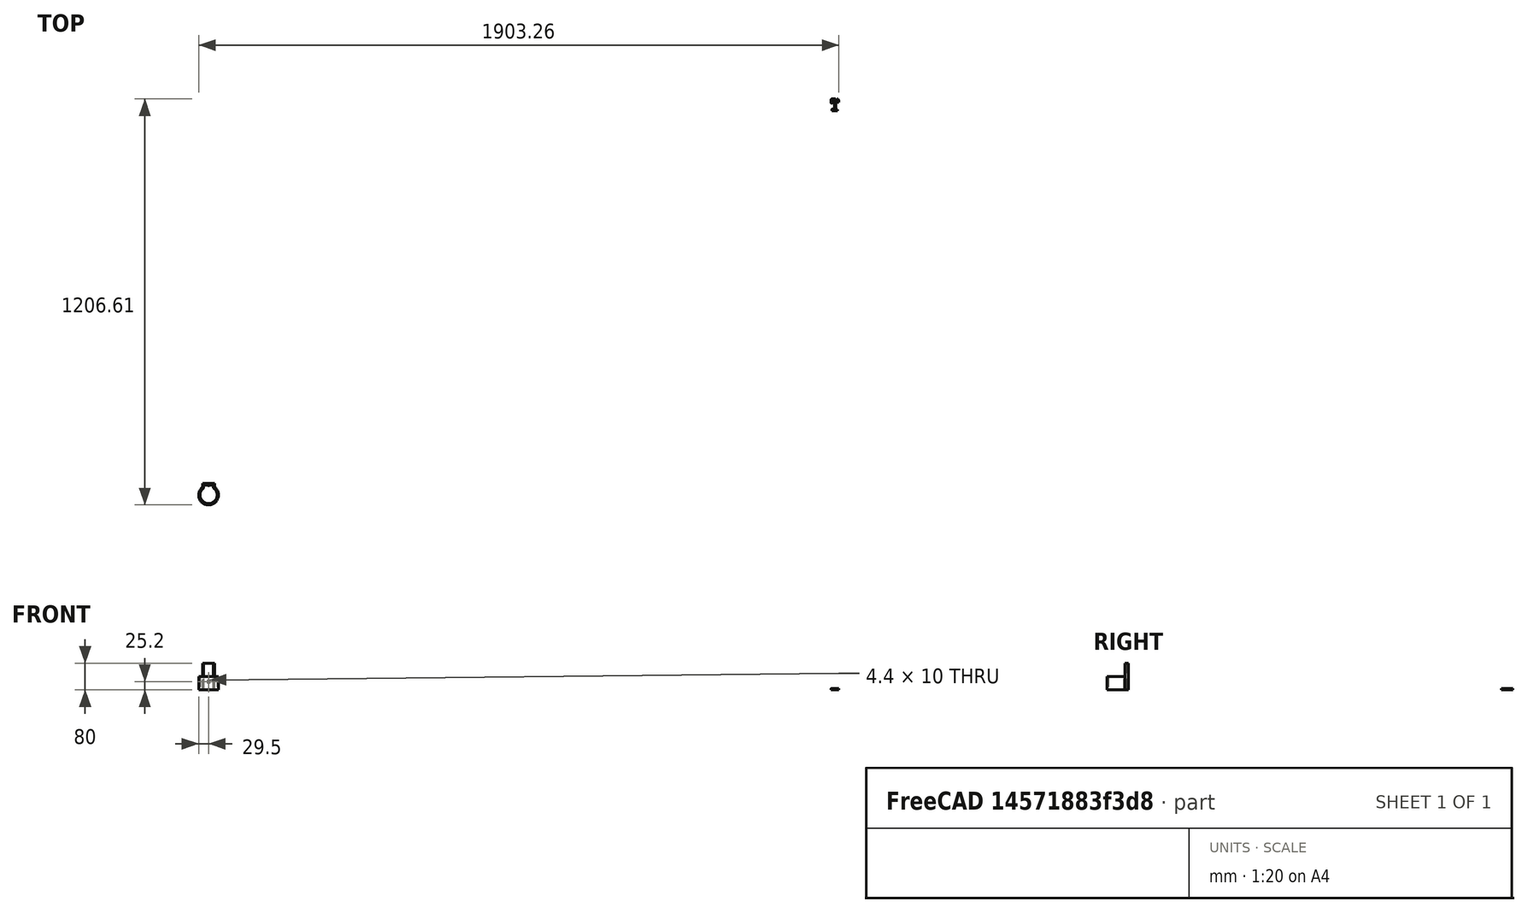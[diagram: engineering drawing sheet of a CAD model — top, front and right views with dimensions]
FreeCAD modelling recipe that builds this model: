
FCSTD DOCUMENT  (FreeCAD 1.2R44861 (Git))
Label: SkadisCylinderHolder
License: All rights reserved
LicenseURL: https://en.wikipedia.org/wiki/All_rights_reserved
objects: PartDesign::Pad×6, Sketcher::SketchObject×5, PartDesign::Pocket×3, Part::Feature×2, PartDesign::Chamfer×2, App::Point×1, Mesh::Feature×1, Part::Refine×1, PartDesign::Body×1
note: 47 computed .brp shape members not serialized (recipe doc carries the construction recipe); baked Part::Feature solids carry a one-line shape summary decoded from their .brp

FEATURE [App::Point] Origin001
  Role = Origin
FEATURE [Mesh::Feature] Skadis_Universal_Hook_1
FEATURE [Part::Feature] Skadis_Universal_Hook_001
  shape: bbox 23.2 x 35 x 4.5 mm, 9836 faces, 0 solids (baked)
FEATURE [Part::Feature] Skadis_Universal_Hook_001_solid  label="Skadis_Universal_Hook_001 (Solid)"
  shape: bbox 23.2 x 35 x 4.5 mm, 9836 faces (baked)
FEATURE [Part::Refine] Skadis_Universal_Hook_001_solid001  label="Skadis_Universal_Hook_001 (Solid)001"
  Source = -> Skadis_Universal_Hook_001_solid
FEATURE [Sketcher::SketchObject] Sketch
  ArcFitTolerance = 1e-06
  AttachmentSupport = -> [Origin]
  ExternalTypes = [0]
  FullyConstrained = true
  MakeInternals = false
  MapMode = 5
  sketch-geometry (4):
    g0: ArcOfCircle CenterX=0 CenterY=0 CenterZ=0 NormalX=0 NormalY=0 NormalZ=1 AngleXU=0 Radius=25.5 StartAngle=2.18166 EndAngle=7.24312
    g1: ArcOfCircle CenterX=0 CenterY=0 CenterZ=0 NormalX=0 NormalY=0 NormalZ=1 AngleXU=0 Radius=29.5 StartAngle=2.08956 EndAngle=7.33522
    g2: LineSegment StartX=-14.6262 StartY=20.8884 StartZ=0 EndX=-14.6262 EndY=25.6188 EndZ=0
    g3: LineSegment StartX=14.6262 StartY=20.8884 StartZ=0 EndX=14.6262 EndY=25.6188 EndZ=0
  constraints (12):
    c: Radius(g0) = 25.5
    c: Angle(g0) = 5.06145
    c: Horizontal(g0,g0)
    c: Coincident(g0,g-1)
    c: Coincident(g1,g0)
    c: Horizontal(g1,g1)
    c: Vertical(g0,g1)
    c: Distance(g1,g0) = 4
    c: Coincident(g2,g0)
    c: Coincident(g2,g1)
    c: Coincident(g3,g0)
    c: Coincident(g3,g1)
FEATURE [PartDesign::Pad] Pad
  Direction = (0,0,1)
  Length = 40
  Length2 = 10
  Profile = -> Sketch
  ReferenceAxis = -> Sketch [N_Axis]
  Refine = true
  SideType = 0
  Suppressed = false
  Type = 0
  Type2 = 0
FEATURE [Sketcher::SketchObject] Sketch001
  ArcFitTolerance = 1e-06
  AttachmentSupport = -> [Origin]
  ExternalGeometry = -> [Pad]
  ExternalTypes = [0]
  FullyConstrained = true
  MakeInternals = false
  MapMode = 5
  sketch-geometry (4):
    g0: LineSegment StartX=-18.1527 StartY=27.8536 StartZ=0 EndX=-18.1527 EndY=23.2536 EndZ=0
    g1: LineSegment StartX=-18.1527 StartY=23.2536 StartZ=0 EndX=18.1527 EndY=23.2536 EndZ=0
    g2: LineSegment StartX=18.1527 StartY=23.2536 StartZ=0 EndX=18.1527 EndY=27.8536 EndZ=0
    g3: LineSegment StartX=18.1527 StartY=27.8536 StartZ=0 EndX=-18.1527 EndY=27.8536 EndZ=0
  constraints (11):
    c: Coincident(g0,g1)
    c: Coincident(g1,g2)
    c: Coincident(g2,g3)
    c: Coincident(g3,g0)
    c: Vertical(g0)
    c: Vertical(g2)
    c: Horizontal(g3)
    c: PointOnObject(g1,g-6)
    c: Symmetric(g-6,g-5,g1)
    c: PointOnObject(g0,g-6)
    c: DistanceY(g0,g0) = 4.6
FEATURE [PartDesign::Pad] Pad001
  BaseFeature = -> Pad
  Direction = (0,0,1)
  Length = 80
  Length2 = 10
  Profile = -> Sketch001
  ReferenceAxis = -> Sketch001 [N_Axis]
  Refine = true
  SideType = 0
  Suppressed = false
  Type = 0
  Type2 = 0
FEATURE [PartDesign::Pad] Pad002
  BaseFeature = -> Pad001
  Direction = (0,0,1)
  Length = 2
  Length2 = 10
  Profile = -> Pad001 [Edge18,Edge28,Edge22,Edge27]
  Refine = true
  SideType = 0
  Suppressed = false
  Type = 0
  Type2 = 0
FEATURE [Sketcher::SketchObject] Sketch002
  ArcFitTolerance = 1e-06
  AttachmentSupport = -> [Pad002]
  ExternalGeometry = -> [Pad002]
  ExternalTypes = [0]
  FullyConstrained = true
  MakeInternals = false
  MapMode = 5
  Placement = pos=(0,27.8536,0) rot=(0,0.707107,0.707107;3.14159rad)
  sketch-geometry (10):
    g0: LineSegment StartX=-2.2 StartY=20.2 StartZ=0 EndX=2.2 EndY=20.2 EndZ=0
    g1: LineSegment StartX=2.2 StartY=20.2 StartZ=0 EndX=2.2 EndY=30.2 EndZ=0
    g2: LineSegment StartX=2.2 StartY=30.2 StartZ=0 EndX=-2.2 EndY=30.2 EndZ=0
    g3: LineSegment StartX=-2.2 StartY=30.2 StartZ=0 EndX=-2.2 EndY=20.2 EndZ=0
    g4: GeomPoint [constr] X=0 Y=25.2 Z=0
    g5: LineSegment StartX=-2.2 StartY=-4.5 StartZ=0 EndX=2.2 EndY=-4.5 EndZ=0
    g6: LineSegment StartX=2.2 StartY=-4.5 StartZ=0 EndX=2.2 EndY=4.5 EndZ=0
    g7: LineSegment StartX=2.2 StartY=4.5 StartZ=0 EndX=-2.2 EndY=4.5 EndZ=0
    g8: LineSegment StartX=-2.2 StartY=4.5 StartZ=0 EndX=-2.2 EndY=-4.5 EndZ=0
    g9: GeomPoint [constr] X=0 Y=0 Z=0
  constraints (25):
    c: Coincident(g0,g1)
    c: Coincident(g1,g2)
    c: Coincident(g2,g3)
    c: Coincident(g3,g0)
    c: Horizontal(g0)
    c: Horizontal(g2)
    c: Vertical(g1)
    c: Vertical(g3)
    c: Symmetric(g2,g0,g4)
    c: PointOnObject(g4,g-2)
    c: Coincident(g5,g6)
    c: Coincident(g6,g7)
    c: Coincident(g7,g8)
    c: Coincident(g8,g5)
    c: Horizontal(g5)
    c: Horizontal(g7)
    c: Vertical(g6)
    c: Vertical(g8)
    c: Symmetric(g7,g5,g9)
    c: Coincident(g9,g-1)
    c: Equal(g0,g7)
    c: Distance(g7,g7) = 4.4
    c: DistanceY(g6,g6) = 9
    c: DistanceY(g1,g1) = 10
    c: DistanceY(g6,g0) = 15.7
FEATURE [PartDesign::Pocket] Pocket
  BaseFeature = -> Pad002
  Direction = (0,-1,2e-16)
  Length = 5
  Length2 = 5
  Profile = -> Sketch002
  ReferenceAxis = -> Sketch002 [N_Axis]
  Refine = true
  SideType = 0
  Suppressed = false
  Type = 0
  Type2 = 0
FEATURE [PartDesign::Pad] Pad003
  BaseFeature = -> Pocket
  Direction = (0,1,0)
  Length = 5
  Length2 = 10
  Profile = -> Pocket [Face4]
  Refine = true
  SideType = 0
  Suppressed = false
  Type = 0
  Type2 = 0
FEATURE [Sketcher::SketchObject] Sketch003
  ArcFitTolerance = 1e-06
  AttachmentSupport = -> [Pad003]
  ExternalGeometry = -> [Pad003]
  ExternalTypes = [0,0]
  FullyConstrained = true
  MakeInternals = false
  MapMode = 5
  Placement = pos=(0,0,80) rot=(0,0,1;0rad)
  sketch-geometry (5):
    g0: Circle [constr] CenterX=0 CenterY=0 CenterZ=0 NormalX=0 NormalY=0 NormalZ=1 AngleXU=0 Radius=25.5
    g1: LineSegment StartX=-14.6262 StartY=23.2536 StartZ=0 EndX=-14.6262 EndY=28.2536 EndZ=0
    g2: LineSegment StartX=-14.6262 StartY=28.2536 StartZ=0 EndX=14.6262 EndY=28.2536 EndZ=0
    g3: LineSegment StartX=14.6262 StartY=28.2536 StartZ=0 EndX=14.6262 EndY=23.2536 EndZ=0
    g4: LineSegment StartX=14.6262 StartY=23.2536 StartZ=0 EndX=-14.6262 EndY=23.2536 EndZ=0
  constraints (12):
    c: Coincident(g0,g-10)
    c: Tangent(g0,g-7)
    c: Coincident(g-12,g1)
    c: Vertical(g1)
    c: Coincident(g1,g2)
    c: Horizontal(g2)
    c: Coincident(g2,g3)
    c: Coincident(g3,g-9)
    c: Coincident(g3,g4)
    c: Coincident(g4,g1)
    c: Vertical(g3)
    c: Distance(g2,g-6) = 4.6
FEATURE [PartDesign::Pocket] Pocket001
  BaseFeature = -> Pad003
  Direction = (0,0,-1)
  Length = 5
  Length2 = 5
  Profile = -> Sketch003
  ReferenceAxis = -> Sketch003 [N_Axis]
  Refine = true
  SideType = 0
  Suppressed = false
  Type = 3
  Type2 = 0
  UpToFace = -> Pad003 [Face4]
FEATURE [Sketcher::SketchObject] Sketch004
  ArcFitTolerance = 1e-06
  AttachmentSupport = -> [Pocket001]
  ExternalGeometry = -> [Pocket001]
  ExternalTypes = [0]
  FullyConstrained = true
  MakeInternals = false
  MapMode = 5
  Placement = pos=(0,0,2) rot=(0,0,1;0rad)
  sketch-geometry (4):
    g0: LineSegment StartX=-2.2 StartY=22.8536 StartZ=0 EndX=2.2 EndY=22.8536 EndZ=0
    g1: LineSegment StartX=2.2 StartY=22.8536 StartZ=0 EndX=2.2 EndY=28.2536 EndZ=0
    g2: LineSegment StartX=2.2 StartY=28.2536 StartZ=0 EndX=-2.2 EndY=28.2536 EndZ=0
    g3: LineSegment StartX=-2.2 StartY=28.2536 StartZ=0 EndX=-2.2 EndY=22.8536 EndZ=0
  constraints (10):
    c: Coincident(g0,g1)
    c: Coincident(g1,g2)
    c: Coincident(g2,g3)
    c: Coincident(g3,g0)
    c: Horizontal(g0)
    c: Horizontal(g2)
    c: Vertical(g1)
    c: Vertical(g3)
    c: Coincident(g0,g-9)
    c: Coincident(g1,g-7)
FEATURE [PartDesign::Pad] Pad004
  BaseFeature = -> Pocket001
  Direction = (0,0,1)
  Length = 10
  Length2 = 10
  Profile = -> Sketch004
  ReferenceAxis = -> Sketch004 [N_Axis]
  Refine = true
  SideType = 0
  Suppressed = false
  Type = 3
  Type2 = 0
  UpToFace = -> Pocket001 [Face4]
FEATURE [PartDesign::Chamfer] Chamfer
  Angle = 85
  Base = -> Pad004 [Edge5]
  BaseFeature = -> Pad004
  ChamferType = 0
  FlipDirection = false
  Refine = true
  Size = 0.5
  Size2 = 30
  SupportTransform = false
  Suppressed = false
  UseAllEdges = false
FEATURE [PartDesign::Pad] Pad005
  BaseFeature = -> Chamfer
  Direction = (0,1,0)
  Length = 1.6
  Length2 = 10
  Profile = -> Chamfer [Face23]
  Refine = true
  SideType = 0
  Suppressed = false
  Type = 0
  Type2 = 0
FEATURE [PartDesign::Pocket] Pocket002
  BaseFeature = -> Pad005
  Direction = (0,1,0)
  Length = 1.5
  Length2 = 5
  Profile = -> Pad005 [Face12]
  Refine = true
  SideType = 0
  Suppressed = false
  Type = 0
  Type2 = 0
FEATURE [PartDesign::Chamfer] Chamfer001
  Angle = 45
  Base = -> Pocket002 [Face5]
  BaseFeature = -> Pocket002
  ChamferType = 0
  FlipDirection = false
  Refine = true
  Size = 1
  Size2 = 1
  SupportTransform = false
  Suppressed = false
  UseAllEdges = false
FEATURE [PartDesign::Body] Body
  AllowCompound = false
  Group = -> [Sketch,Pad,Sketch001,Pad001,Pad002,Sketch002,Pocket,Pad003,Sketch003,Pocket001,Sketch004,Pad004,Chamfer,Pad005,Pocket002,Chamfer001]
  Origin = -> Origin
  Tip = -> Chamfer001
